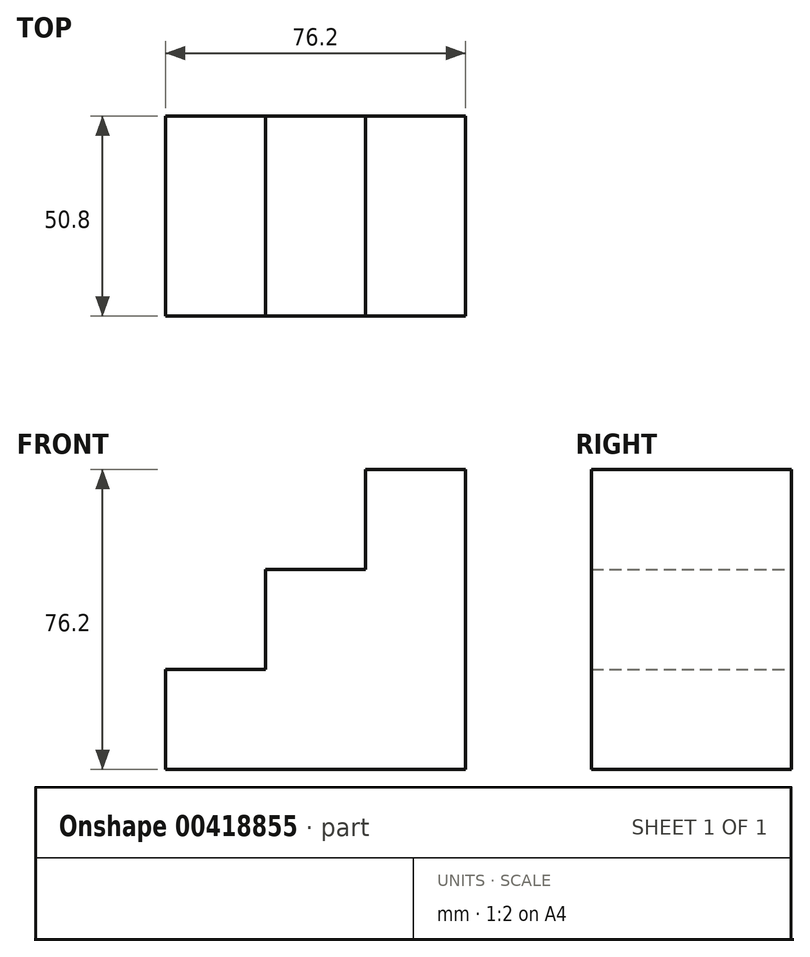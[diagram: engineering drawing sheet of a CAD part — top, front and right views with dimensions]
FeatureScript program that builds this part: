
annotation { "Feature Type Name" : "Feature", "Feature Type Description" : "" }
export const myFeature = defineFeature(function(context is Context, id is Id, definition is map)
    precondition{}
    {
        {
            var Q0;
            Q0=qCreatedBy(makeId("Front.planeOp"),FACE);
            var sketch = newSketch(context, id + "F0", { "sketchPlane" : qUnion([Q0])});
            skLineSegment(sketch, "E0", {"start": v(0, 0) * mm, "end": v(-76.2, 0) * mm});
            skLineSegment(sketch, "E1", {"start": v(-76.2, 0) * mm, "end": v(-76.2, 25.4) * mm});
            skLineSegment(sketch, "E2", {"start": v(-76.2, 25.4) * mm, "end": v(-50.8, 25.4) * mm});
            skLineSegment(sketch, "E3", {"start": v(-50.8, 25.4) * mm, "end": v(-50.8, 50.8) * mm});
            skLineSegment(sketch, "E4", {"start": v(-50.8, 50.8) * mm, "end": v(-25.4, 50.8) * mm});
            skLineSegment(sketch, "E5", {"start": v(-25.4, 50.8) * mm, "end": v(-25.4, 76.2) * mm});
            skLineSegment(sketch, "E6", {"start": v(-25.4, 76.2) * mm, "end": v(0, 76.2) * mm});
            skLineSegment(sketch, "E7", {"start": v(0, 0) * mm, "end": v(0, 76.2) * mm});
            skSolve(sketch);
        }
        {
            var Q0;
            Q0 = qSketchRegion(id + "F0", true);
            extrude(context, id + "F1", {"entities" : qUnion([Q0]), "depth" : 50.8 * mm});
        }
    });
